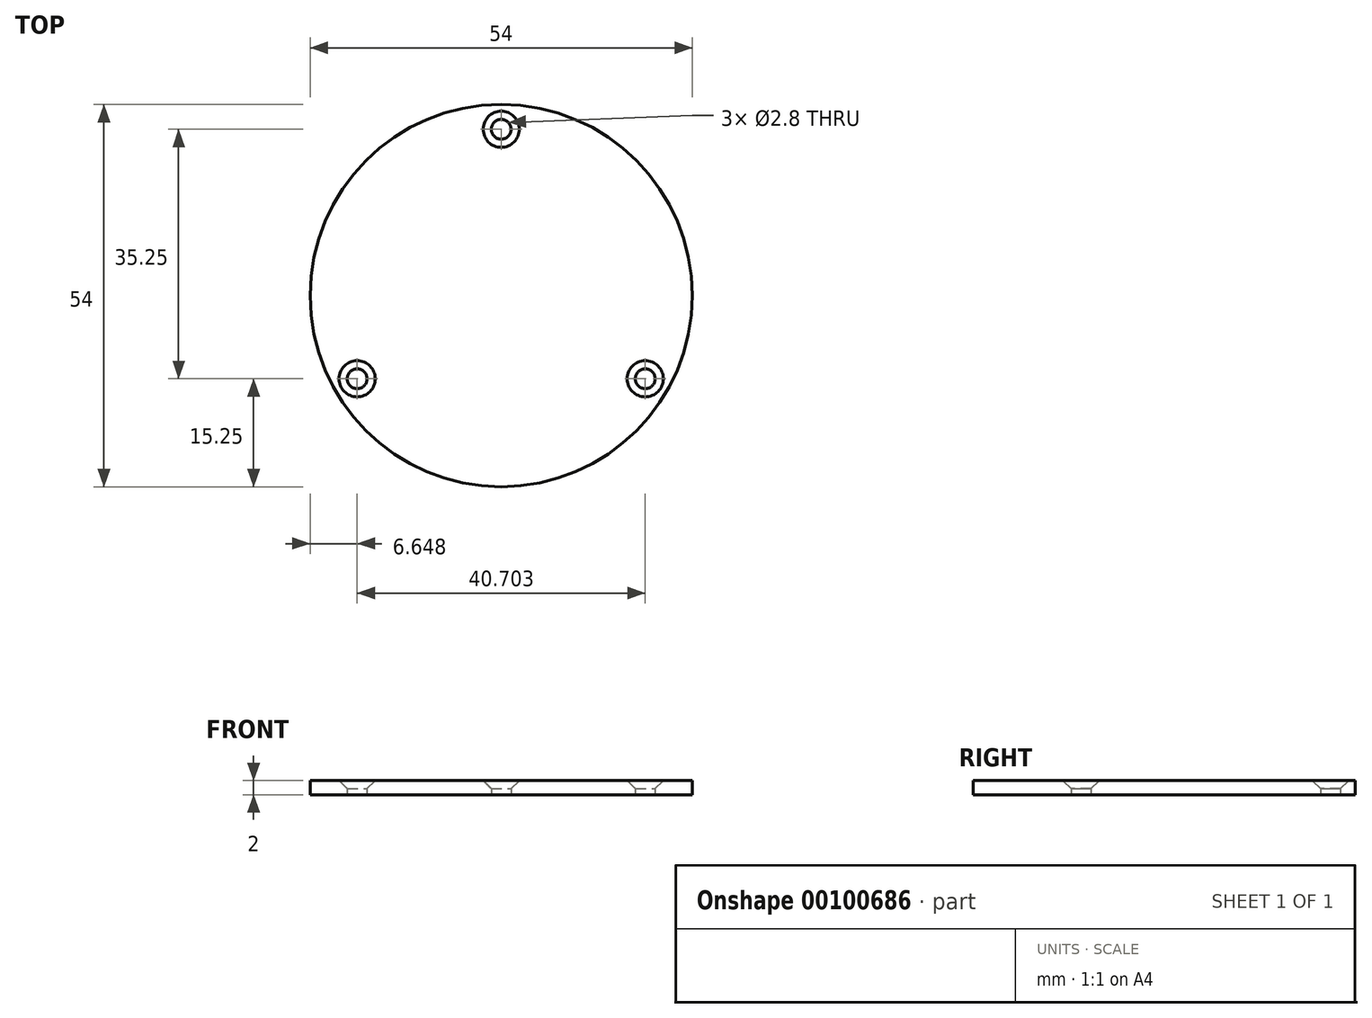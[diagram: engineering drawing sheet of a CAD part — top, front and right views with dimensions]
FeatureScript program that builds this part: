
annotation { "Feature Type Name" : "Feature", "Feature Type Description" : "" }
export const myFeature = defineFeature(function(context is Context, id is Id, definition is map)
    precondition{}
    {
        {
            var Q0;
            Q0=qCreatedBy(makeId("Top.planeOp"),FACE);
            var sketch = newSketch(context, id + "F0", { "sketchPlane" : qUnion([Q0])});
            skCircle(sketch, "E0", {"center": v(0, 0) * mm, "radius": 27 * mm});
            skSolve(sketch);
        }
        {
            var Q0;
            Q0 = qSketchRegion(id + "F0", true);
            extrude(context, id + "F1", {"entities" : qUnion([Q0]), "depth" : 2 * mm});
        }
        {
            var Q0;
            Q0=makeQuery(id+"F1.opExtrude","CAP_FACE",FACE,{"disambiguationData":[OSD([sQuery(id+"F0.wireOp",EDGE,"E0")])],"isStart":false});
            var sketch = newSketch(context, id + "F2", { "sketchPlane" : qUnion([Q0])});
            skLineSegment(sketch, "E1", {"start": v(0, 0) * mm, "end": v(0, 23.5) * mm, "construction": true});
            skLineSegment(sketch, "E2.1.0", {"start": v(0, 0) * mm, "end": v(-20.35, -11.75) * mm, "construction": true});
            skLineSegment(sketch, "E2.2.0", {"start": v(0, 0) * mm, "end": v(20.35, -11.75) * mm, "construction": true});
            skPoint(sketch, "E2.center", {"position": v(0, 0) * mm});
            skSolve(sketch);
        }
        {
            var Q0;
            Q0=sQuery(id+"F2.wireOp",VERTEX,"E1.end");
            var Q1;
            Q1=sQuery(id+"F2.wireOp",VERTEX,"E2.1.0.end");
            var Q2;
            Q2=sQuery(id+"F2.wireOp",VERTEX,"E2.2.0.end");
            var Q3;
            Q3=makeQuery(id+"F1.opExtrude","SWEPT_BODY",BODY,{"disambiguationData":[OSD([sQuery(id+"F0.wireOp",EDGE,"E0")])]});
            hole(context, id + "F3", {"style" : HoleStyle.C_SINK, "endStyle" : HoleEndStyle.THROUGH, "holeDiameter" : 2.8 * mm, "cSinkDiameter" : 5.1 * mm, "cSinkAngle" : 90 * degree, "locations" : qUnion([Q0, Q1, Q2]), "scope" : qUnion([Q3]), "isTappedThrough" : true, "startStyle" : HoleStartStyle.PART});
        }
    });
